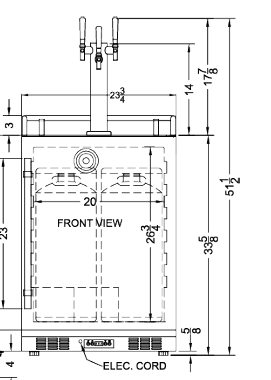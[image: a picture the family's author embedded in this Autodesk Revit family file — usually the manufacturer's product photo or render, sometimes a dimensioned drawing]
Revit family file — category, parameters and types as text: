
# Revit family: QF_Summit_BC74OSCOM_Single_Tap_Beer_Dispenser
name_source: partatom
category: Specialty Equipment
units: mm (PartAtom-declared; Revit-internal decimal feet)

## family parameters
Always vertical = Yes
Cut with Voids When Loaded = No
Part Type = Normal
Room Calculation Point = No
Round Connector Dimension = Use Diameter
Shared = No
Work Plane-Based = No

## types (1)
- QF_Summit_BC74OSCOM_Single_Tap_Beer_Dispenser
    Apparent Power = 144 VA
    BTUH = 0.0 Btu/h
    Conn Conduit = Yes
    Cycle = 60 Hz
    Default Elevation = 0"
    Depth = 24 1/4"
    Description = Single Tap Beer Dispenser
    Elec Conn Connection Height = 0"
    Elec Conn RI Height = 0"
    FL Amps = 1 A
    Foodservice Equipment Identifier = Yes
    Identify Quantity as Lot = Yes
    Length = 23 3/4"
    Manufacturer = Summit
    Max Overcurrent Protection = 0 A
    Min Ckt Ampacity = 0 A
    Model = BC74OSCOM
    Number of Poles = 1
    Phase = 1
    Refrigerant Type = R600a
    Refrigerant Volume = 0.00 kip
    Volts = 115 V
    Watts = 144 W
    Weight in Pounds = 120

## geometry (parser evidence)
native form markers: Blend x4, Sweep x23
no freeform markers — native parametric forms only
